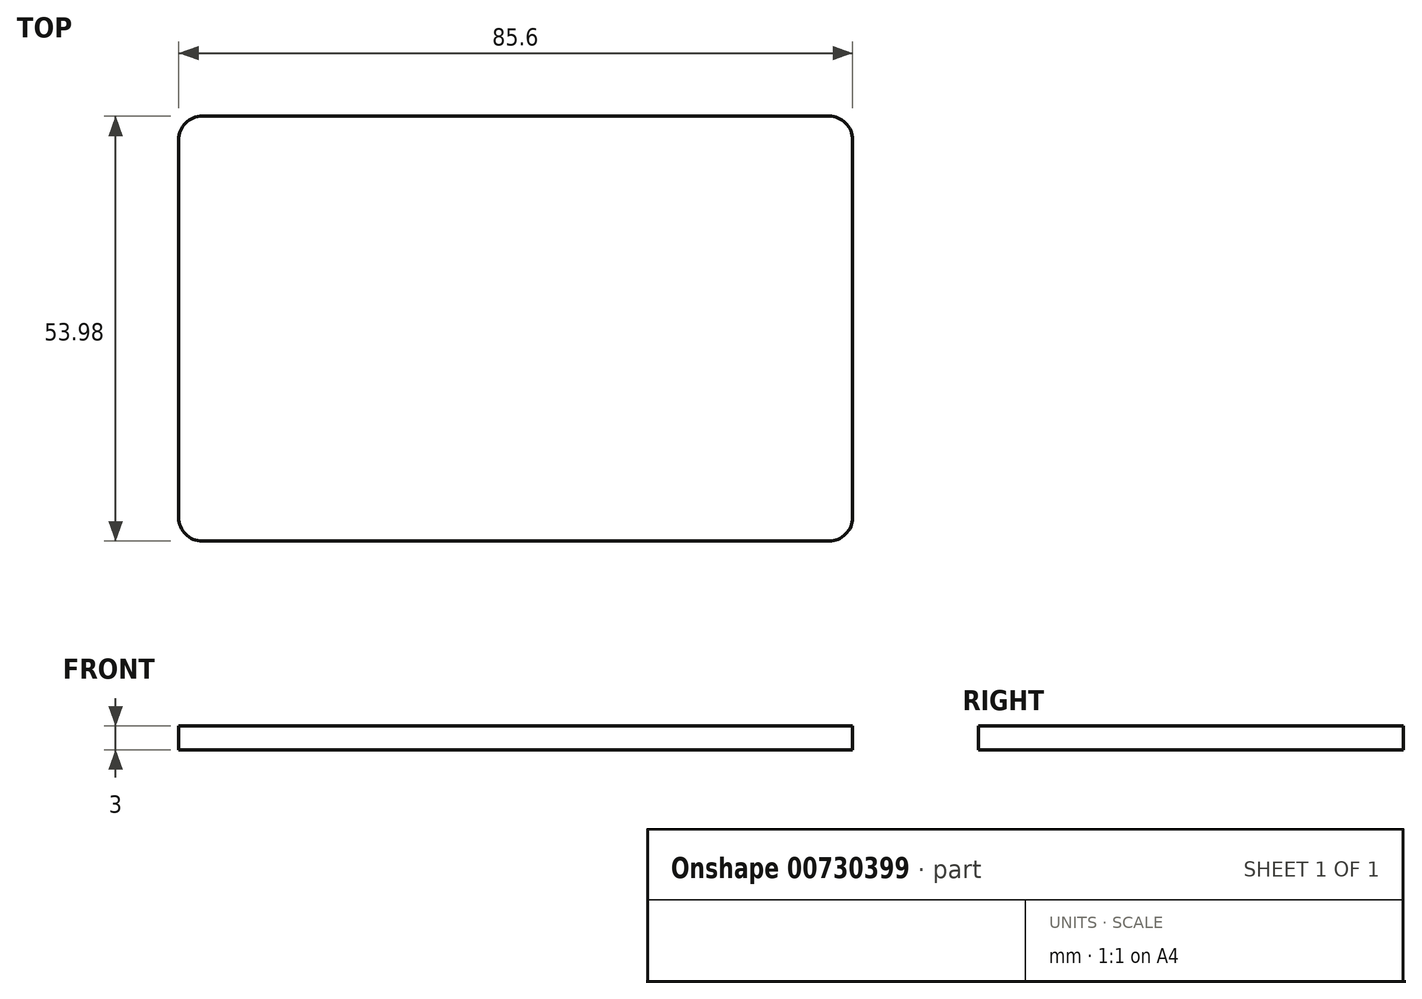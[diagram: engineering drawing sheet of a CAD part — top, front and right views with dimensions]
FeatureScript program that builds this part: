
annotation { "Feature Type Name" : "Feature", "Feature Type Description" : "" }
export const myFeature = defineFeature(function(context is Context, id is Id, definition is map)
    precondition{}
    {
        {
            var Q0;
            Q0=qCreatedBy(makeId("Top.planeOp"),FACE);
            var sketch = newSketch(context, id + "F0", { "sketchPlane" : qUnion([Q0])});
            skLineSegment(sketch, "E0.bottom", {"start": v(-39.8, 26.99) * mm, "end": v(39.8, 26.99) * mm});
            skLineSegment(sketch, "E0.top", {"start": v(-39.8, -26.99) * mm, "end": v(39.8, -26.99) * mm});
            skLineSegment(sketch, "E0.left", {"start": v(-42.8, 23.99) * mm, "end": v(-42.8, -24) * mm});
            skLineSegment(sketch, "E0.right", {"start": v(42.8, 23.99) * mm, "end": v(42.8, -24) * mm});
            skPoint(sketch, "E0.middle", {"position": v(0, 0) * mm});
            skPoint(sketch, "E1.visualSharp", {"position": v(-42.8, 26.99) * mm});
            skArc(sketch, "E1.filletArc", {"start": v(-39.8, 26.99) * mm, "mid": v(-41.92, 26.11) * mm, "end": v(-42.8, 23.99) * mm});
            skPoint(sketch, "E2.visualSharp", {"position": v(42.8, 26.99) * mm});
            skArc(sketch, "E2.filletArc", {"start": v(42.8, 23.99) * mm, "mid": v(41.92, 26.11) * mm, "end": v(39.8, 26.99) * mm});
            skPoint(sketch, "E3.visualSharp", {"position": v(42.8, -26.99) * mm});
            skArc(sketch, "E3.filletArc", {"start": v(39.8, -26.99) * mm, "mid": v(41.92, -26.11) * mm, "end": v(42.8, -24) * mm});
            skPoint(sketch, "E4.visualSharp", {"position": v(-42.8, -26.99) * mm});
            skArc(sketch, "E4.filletArc", {"start": v(-42.8, -24) * mm, "mid": v(-41.92, -26.11) * mm, "end": v(-39.8, -26.99) * mm});
            skSolve(sketch);
        }
        {
            var Q0;
            Q0=makeQuery(id+"F0.imprint","IMPRINT",FACE,{"disambiguationData":[TD([[makeQuery(id+"F0.imprint","IMPRINT",EDGE,{"derivedFrom":sQuery(id+"F0.wireOp",EDGE,"E0.bottom")}),-1.0]])]});
            extrude(context, id + "F1", {"entities" : qUnion([Q0]), "depth" : 3 * mm, "offsetDistance" : 25 * mm});
        }
    });
